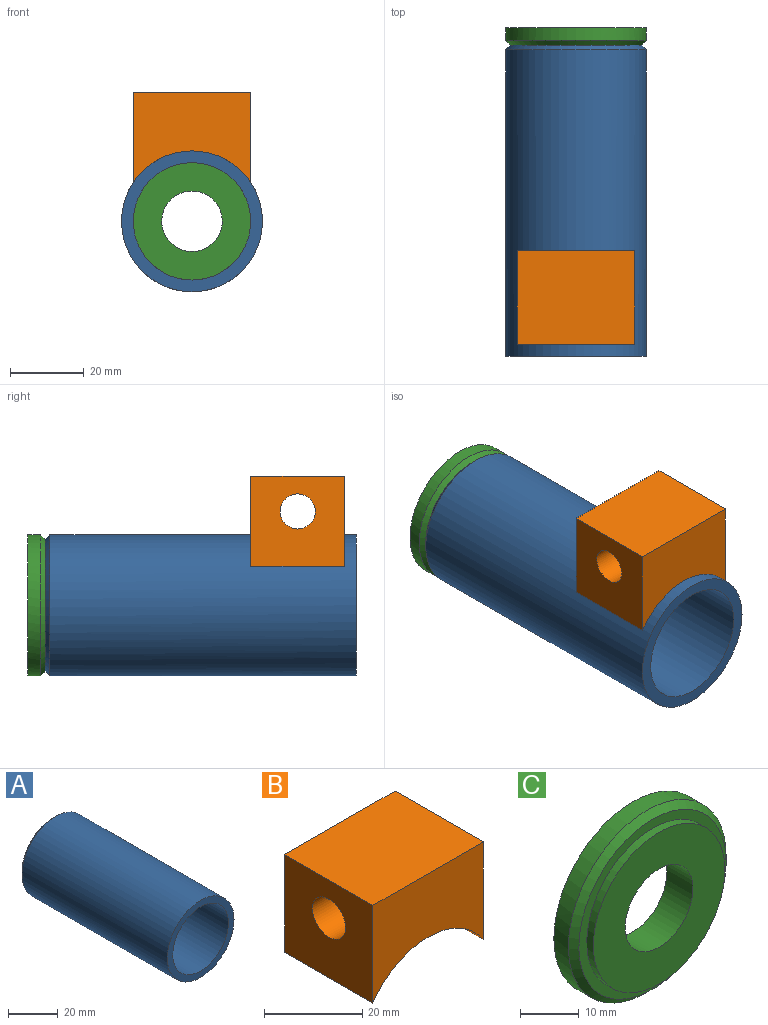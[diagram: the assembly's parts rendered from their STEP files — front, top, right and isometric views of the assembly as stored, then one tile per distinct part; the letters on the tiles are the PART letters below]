
ASSEMBLY  parts=3 mates=2
PART A: 5 faces, bbox 38.1x84.1x38.1 mm
  f0: plane 35.56x35.56mm, normal (0,1,0), area 201.4mm2, adj f3,f4
  f1: cylinder r=19.05mm len=82.87mm, axis (0,1,0), area 9918.8mm2, adj f2,f4
  f2: plane 38.1x38.1mm, normal (0,-1,0), area 348.4mm2, adj f1,f3
  f3: cylinder r=15.88mm len=84.14mm, axis (0,-1,0), area 8392.3mm2, adj f0,f2
  f4: cone r=17.78mm half-angle=45deg, axis (0,-1,0), area 207.8mm2, adj f0,f1
PART B: 7 faces, bbox 31.8x25.4x24.4 mm
  f0: plane 31.75x24.39mm, normal (0,1,0), area 584.2mm2, adj f1,f2,f3,f4
  f1: plane 25.4x24.39mm, normal (1,0,0), area 548.4mm2, adj f0,f2,f3,f5,f6
  f2: plane 31.75x25.4mm, normal (0,0,1), area 806.5mm2, adj f0,f1,f4,f5
  f3: cylinder r=19.05mm len=31.75mm, axis (0,-1,0), area 953.3mm2, adj f0,f1,f4,f5
  f4: plane 25.4x24.39mm, normal (-1,0,0), area 548.4mm2, adj f0,f2,f3,f5,f6
  f5: plane 31.75x24.39mm, normal (0,-1,0), area 584.2mm2, adj f1,f2,f3,f4
  f6: cylinder r=4.76mm len=31.75mm, axis (1,0,0), area 950.1mm2, adj f1,f4
PART C: 7 faces, bbox 38.1x6.4x38.1 mm
  f0: cylinder r=19.05mm len=38.1mm, axis (0,1,0), area 418mm2, adj f1,f6
  f1: plane 38.1x38.1mm, normal (0,1,0), area 929.3mm2, adj f0,f3
  f2: plane 35.56x35.56mm, normal (0,-1,0), area 201.4mm2, adj f4,f6
  f3: cylinder r=8.19mm len=16.38mm, axis (0,1,0), area 326.8mm2, adj f1,f5
  f4: cylinder r=15.88mm len=31.75mm, axis (0,1,0), area 158.3mm2, adj f2,f5
  f5: plane 31.75x31.75mm, normal (0,-1,0), area 580.9mm2, adj f3,f4
  f6: cone r=19.05mm half-angle=45deg, axis (0,1,0), area 207.8mm2, adj f0,f2
PLACE A at identity fixed
PLACE B t=(0,0.63,0)mm
PLACE C at identity
MATE fastened A.f1 <-> C.f0  axis (0,1,0) through (0,-4.76,0)mm
MATE fastened A.f1 <-> B.f3  axis (0,-1,0) through (0,-88.9,0)mm
